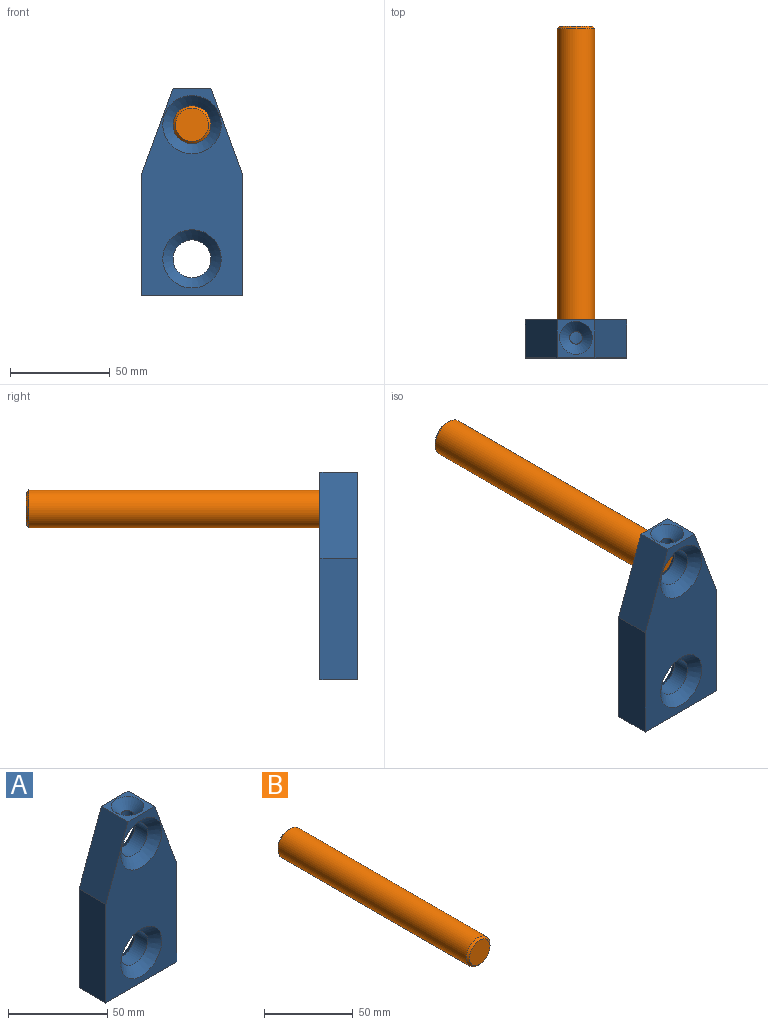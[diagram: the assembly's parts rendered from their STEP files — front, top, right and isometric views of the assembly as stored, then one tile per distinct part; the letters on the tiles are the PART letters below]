
ASSEMBLY  parts=2 mates=1
PART A: 16 faces, bbox 50.8x19x104.1 mm
  f0: cylinder r=9.53mm len=19.05mm, axis (0,-1,0), area 496.8mm2, adj f10,f11,f14
  f1: plane 19.05x19mm, normal (0,0,1), area 147.9mm2, adj f2,f6,f7,f8,f15
  f2: plane 43.18x19mm, normal (-0.94,0,0.35), area 874.1mm2, adj f1,f3,f7,f8
  f3: plane 60.96x19mm, normal (-1,0,0), area 1158.2mm2, adj f2,f4,f7,f8
  f4: plane 50.8x19mm, normal (0,0,-1), area 965.2mm2, adj f3,f5,f7,f8
  f5: plane 60.96x19mm, normal (1,0,0), area 1158.2mm2, adj f4,f6,f7,f8
  f6: plane 43.18x19mm, normal (0.94,0,0.35), area 874.1mm2, adj f1,f5,f7,f8
  f7: plane 104.14x50.8mm, normal (0,-1,0), area 3264.6mm2, adj f1,f2,f3,f4,f5,f6,f11,f12
  f8: plane 104.14x50.8mm, normal (0,1,0), area 3264.6mm2, adj f1,f2,f3,f4,f5,f6,f13,f14
  f9: cylinder r=9.53mm len=19.05mm, axis (0,-1,0), area 529mm2, adj f12,f13
  f10: cylinder r=3.17mm len=6.35mm, axis (0,0,1), area 79.4mm2, adj f0,f15
  f11: cone r=9.53mm half-angle=45deg, axis (0,-1,0), area 544.6mm2, adj f0,f7
  f12: cone r=9.53mm half-angle=45deg, axis (0,-1,0), area 544.6mm2, adj f7,f9
  f13: cone r=9.53mm half-angle=45deg, axis (0,1,0), area 544.6mm2, adj f8,f9
  f14: cone r=9.53mm half-angle=45deg, axis (0,1,0), area 544.6mm2, adj f0,f8
  f15: cone r=3.17mm half-angle=45deg, axis (0,0,1), area 258mm2, adj f1,f10
PART B: 5 faces, bbox 19.1x152.4x19.1 mm
  f0: cylinder r=9.53mm len=149.86mm, axis (0,1,0), area 8968.7mm2, adj f3,f4
  f1: plane 16.51x16.51mm, normal (0,-1,0), area 214.1mm2, adj f3
  f2: plane 16.51x16.51mm, normal (0,1,0), area 214.1mm2, adj f4
  f3: cone r=8.26mm half-angle=45deg, axis (0,1,0), area 100.3mm2, adj f0,f1
  f4: cone r=9.53mm half-angle=45deg, axis (0,-1,0), area 100.3mm2, adj f0,f2
PLACE A t=(-28.94,33.03,5.02)mm
PLACE B t=(-295.39,180.35,-21.05)mm
MATE slider B.f0 <-> A.f0  axis (0,-1,0) through (-122,27.95,74.14)mm
